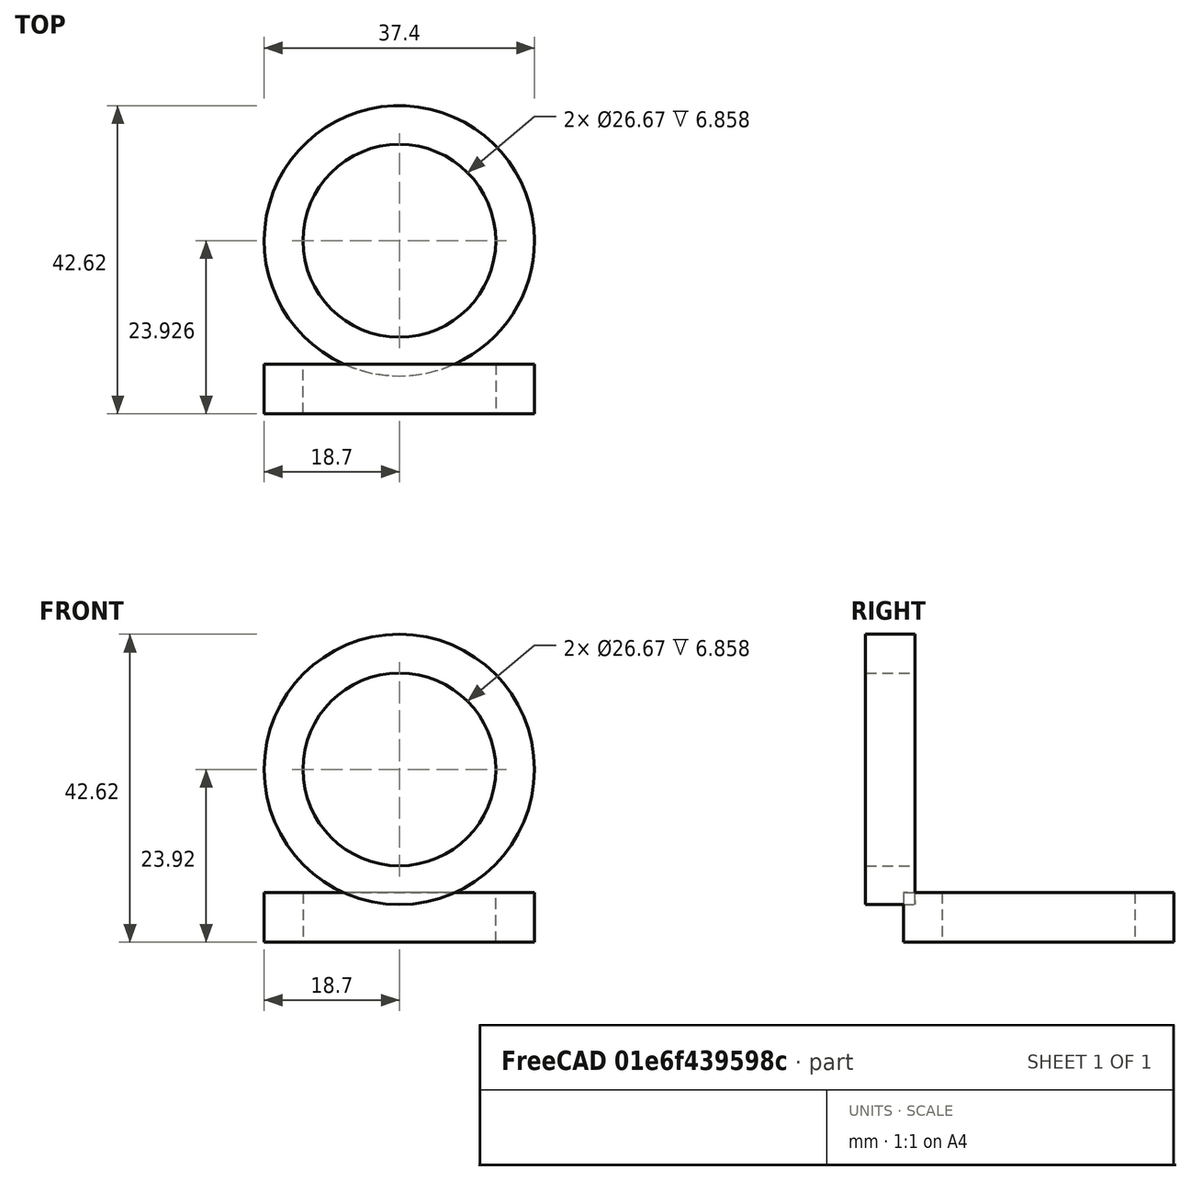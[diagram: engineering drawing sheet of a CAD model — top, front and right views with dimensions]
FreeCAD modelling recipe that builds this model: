
FCSTD DOCUMENT  (FreeCAD 0.16R6712 (Git))
Label: 0.75in NPT 90 elbow
License: CreativeCommons Attribution-ShareAlike
LicenseURL: http://creativecommons.org/licenses/by-sa/4.0/
objects: Part::FeaturePython×4, Part::Circle×3, App::FeaturePython×3, Part::Sweep×2, Sketcher::SketchObject×1, PartDesign::Pad×1, Part::Feature×1
note: 13 computed .brp shape members not serialized (recipe doc carries the construction recipe); baked Part::Feature solids carry a one-line shape summary decoded from their .brp

FEATURE [Part::Circle] Base  label="ID"
  Angle0 = 0
  Angle1 = 360
  Placement = pos=(0,0,-17.0656) rot=(0,0,1;0rad)
  Radius = 13.335
FEATURE [Part::Circle] Trajectory  label="Trajectory 90 elbow"
  Angle0 = 90
  Angle1 = 180
  Placement = pos=(17.0656,0,-17.0656) rot=(1,0,0;1.5708rad)
  Radius = 17.0656
FEATURE [Part::Sweep] Sweep  label="inner"
  Frenet = false
  Sections = -> [Base]
  Solid = false
  Spine = -> Trajectory
  Transition = 1
FEATURE [Part::Circle] Base001  label="OD"
  Angle0 = 0
  Angle1 = 360
  Placement = pos=(0,0,-17.0656) rot=(0,0,1;0rad)
  Radius = 16.7904
FEATURE [Part::Sweep] Sweep001  label="outer"
  Frenet = false
  Sections = -> [Base001]
  Solid = false
  Spine = -> Trajectory [Edge1]
  Transition = 1
FEATURE [Sketcher::SketchObject] Sketch002  label="thread end "
  Placement = pos=(101.6,-330.2,-127) rot=(1,0,0;1.5708rad)
  sketch-geometry (2):
    g0: Circle CenterX=0 CenterY=0 CenterZ=0 NormalX=0 NormalY=0 NormalZ=1 Radius=13.335
    g1: Circle CenterX=0 CenterY=0 CenterZ=0 NormalX=0 NormalY=0 NormalZ=1 Radius=18.6954
  constraints (4):
    c: Coincident(g0,g-1)
    c: Radius(g0) = 13.335
    c: Coincident(g1,g-1)
    c: Radius(g1) = 18.6954
FEATURE [PartDesign::Pad] Pad  label="End"
  Length = 6.858
  Length2 = 100
  Placement = pos=(101.6,-330.2,-127) rot=(1,0,0;1.5708rad)
  Sketch = -> Sketch002
  Type = 0
FEATURE [Part::FeaturePython] Clone  label="Clone of outer"  # Draft clone (typed FeaturePython)
  Objects = -> [Sweep001]
  Placement = pos=(0,-236.934,0) rot=(0,0,-1;1.5708rad)
  Scale = (1,1,1)
FEATURE [Part::FeaturePython] Clone001  label="Clone of inner"  # Draft clone (typed FeaturePython)
  Objects = -> [Sweep]
  Placement = pos=(0,-236.934,0) rot=(0,0,-1;1.5708rad)
  Scale = (1,1,1)
FEATURE [Part::FeaturePython] Clone002  label="Clone of End"  # Draft clone (typed FeaturePython)
  Objects = -> [Pad]
  Placement = pos=(0,-254,0) rot=(1,0,0;1.5708rad)
  Scale = (1,1,1)
FEATURE [Part::FeaturePython] Clone003  label="Clone of End001"  # Draft clone (typed FeaturePython)
  Objects = -> [Pad]
  Placement = pos=(0,-236.934,-23.9236) rot=(0,0,1;0rad)
  Scale = (1,1,1)
FEATURE [App::FeaturePython] circularEdgeConstraint01  # a2plus constraint (typed FeaturePython)
  Object1 = Clone002
  Object2 = Clone001
  SubElement1 = Edge5
  SubElement2 = Edge2
  Type = circularEdge
  directionConstraint = 0
  lockRotation = false
  offset = 0
FEATURE [App::FeaturePython] circularEdgeConstraint02  # a2plus constraint (typed FeaturePython)
  Object1 = Clone
  Object2 = Clone002
  SubElement1 = Edge2
  SubElement2 = Edge2
  Type = circularEdge
  directionConstraint = 0
  lockRotation = false
  offset = 0
FEATURE [App::FeaturePython] circularEdgeConstraint03  # a2plus constraint (typed FeaturePython)
  Object1 = Clone003
  Object2 = Clone001
  SubElement1 = Edge6
  SubElement2 = Edge3
  Type = circularEdge
  directionConstraint = 0
  lockRotation = false
  offset = 0
FEATURE [Part::Feature] Compound001  label="0.75in NPT 90 elbow"
  shape: bbox 37.39 x 43.5 x 43.5 mm, 10 faces, 2 solids (baked)
